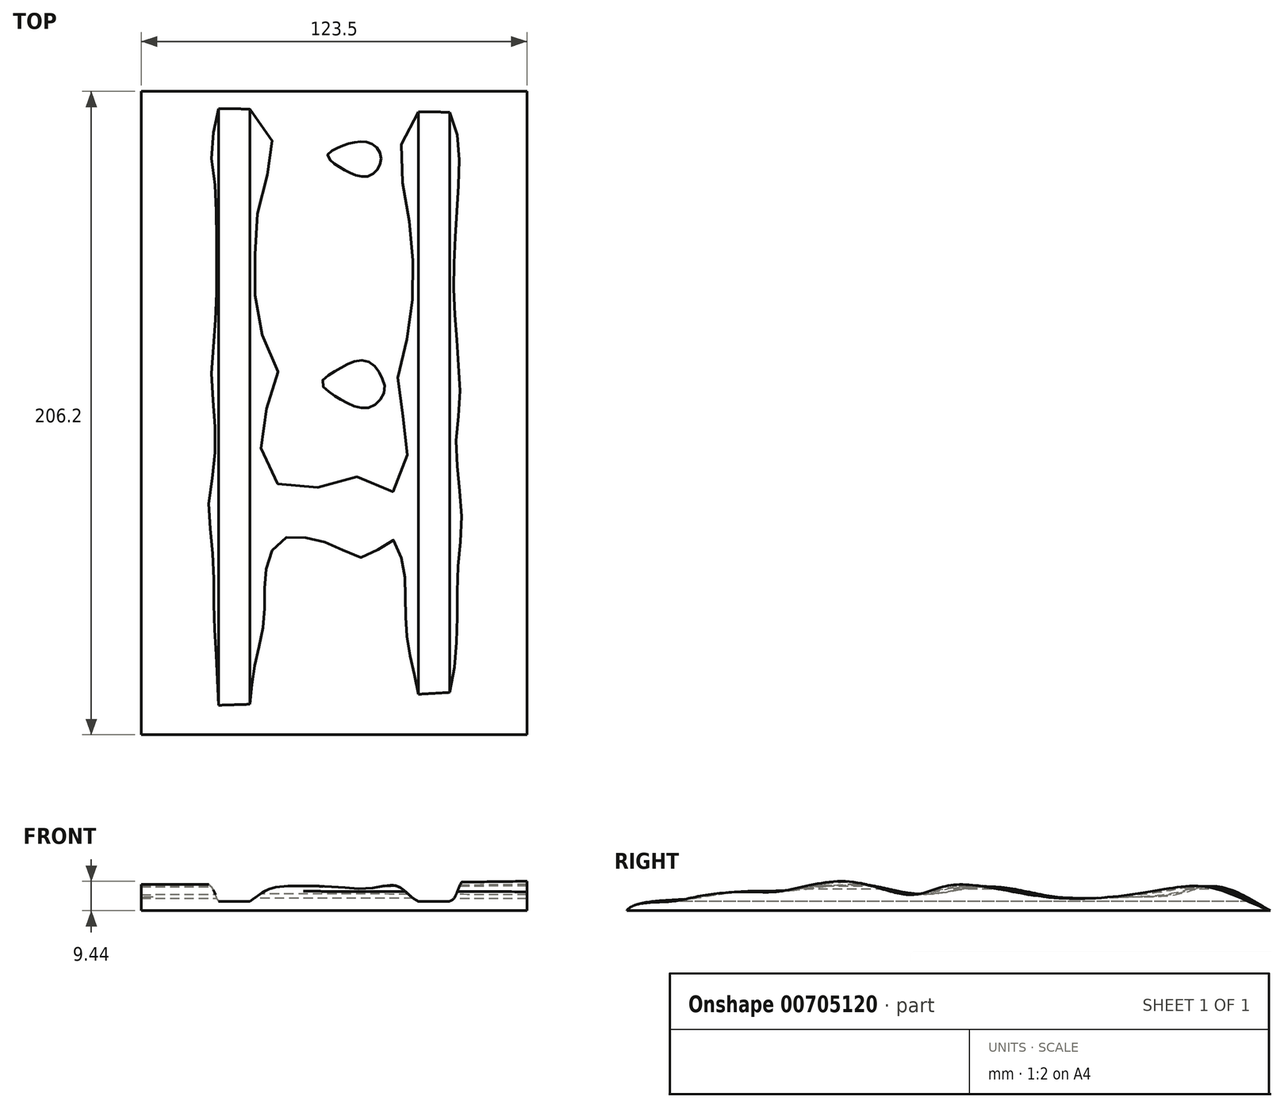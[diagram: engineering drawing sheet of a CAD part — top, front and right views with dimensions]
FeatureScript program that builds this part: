
annotation { "Feature Type Name" : "Feature", "Feature Type Description" : "" }
export const myFeature = defineFeature(function(context is Context, id is Id, definition is map)
    precondition{}
    {
        {
            var Q0;
            Q0=qCreatedBy(makeId("Top.planeOp"),FACE);
            var sketch = newSketch(context, id + "F0", { "sketchPlane" : qUnion([Q0])});
            skLineSegment(sketch, "E0.bottom", {"start": v(-61.75, 103.1) * mm, "end": v(61.75, 103.1) * mm});
            skLineSegment(sketch, "E0.top", {"start": v(-61.75, -103.1) * mm, "end": v(61.75, -103.1) * mm});
            skLineSegment(sketch, "E0.left", {"start": v(-61.75, 103.1) * mm, "end": v(-61.75, -103.1) * mm});
            skLineSegment(sketch, "E0.right", {"start": v(61.75, 103.1) * mm, "end": v(61.75, -103.1) * mm});
            skLineSegment(sketch, "E1", {"start": v(-61.75, -103.1) * mm, "end": v(61.75, 103.1) * mm, "construction": true});
            skSolve(sketch);
        }
        {
            var Q0;
            Q0=qCreatedBy(makeId("Right.planeOp"),FACE);
            var Q1;
            Q1=sQuery(id+"F0.wireOp",VERTEX,"E0.top.end");
            cPlane(context, id + "F1", {"entities" : qUnion([Q0, Q1]), "cplaneType" : CPlaneType.PLANE_POINT, "offset" : 25 * mm, "width" : 150 * mm, "height" : 150 * mm});
        }
        {
            var Q0;
            Q0=qCreatedBy(makeId("Right.planeOp"),FACE);
            var Q1;
            Q1=sQuery(id+"F0.wireOp",VERTEX,"E1.start");
            cPlane(context, id + "F2", {"entities" : qUnion([Q0, Q1]), "cplaneType" : CPlaneType.PLANE_POINT, "offset" : 25 * mm, "width" : 150 * mm, "height" : 150 * mm});
        }
        {
            var Q0;
            Q0=qCreatedBy(makeId("Front.planeOp"),FACE);
            var Q1;
            Q1=sQuery(id+"F0.wireOp",VERTEX,"E0.top.end");
            cPlane(context, id + "F3", {"entities" : qUnion([Q0, Q1]), "cplaneType" : CPlaneType.PLANE_POINT, "offset" : 25 * mm, "width" : 150 * mm, "height" : 150 * mm});
        }
        {
            var Q0;
            Q0=qCreatedBy(id+"F1.planeOp",FACE);
            var sketch = newSketch(context, id + "F4", { "sketchPlane" : qUnion([Q0])});
            skPoint(sketch, "E2.0", {"position": v(-103.1, 0) * mm});
            skLineSegment(sketch, "E3.0", {"start": v(103.1, 0) * mm, "end": v(-103.1, 0) * mm});
            skFitSpline(sketch, "E4", {"points": [v(-103.1, 0) * mm, v(-90, 2.88) * mm, v(-79.4, 4.75) * mm, v(-64.63, 6.07) * mm, v(-53.4, 6.3) * mm, v(-32.22, 9.37) * mm, v(-12.09, 5.07) * mm, v(1.58, 8.28) * mm, v(32.22, 4.27) * mm, v(65.38, 6.24) * mm, v(83.82, 7.43) * mm, v(103.1, 0) * mm], "startDerivative": vector(84.6, 116.32) * mm, "endDerivative": vector(192.63, -70.23) * mm});
            skSolve(sketch);
        }
        {
            var Q0;
            Q0=qCreatedBy(id+"F2.planeOp",FACE);
            var sketch = newSketch(context, id + "F5", { "sketchPlane" : qUnion([Q0])});
            skLineSegment(sketch, "E5.0", {"start": v(103.1, 0) * mm, "end": v(-103.1, 0) * mm});
            skFitSpline(sketch, "E6", {"points": [v(103.1, 0) * mm, v(85.95, 7.8) * mm, v(73.38, 5.16) * mm, v(56.6, 4.36) * mm, v(34.64, 4.36) * mm, v(13.21, 7.67) * mm, v(-8.2, 5.16) * mm, v(-27.25, 8.33) * mm, v(-48.4, 6.61) * mm, v(-66.4, 6.08) * mm, v(-84.38, 3.7) * mm, v(-103.1, 0) * mm], "startDerivative": vector(-178.89, 101.55) * mm, "endDerivative": vector(-86.83, -108.74) * mm});
            skSolve(sketch);
        }
        {
            var Q0;
            Q0=makeQuery(id+"F4.imprint","IMPRINT",FACE,{"disambiguationData":[TD([[makeQuery(id+"F4.imprint","IMPRINT",EDGE,{"derivedFrom":sQuery(id+"F4.wireOp",EDGE,"E3.0")}),-1.0]])]});
            var Q1;
            Q1=makeQuery(id+"F5.imprint","IMPRINT",FACE,{"disambiguationData":[TD([[makeQuery(id+"F5.imprint","IMPRINT",EDGE,{"derivedFrom":sQuery(id+"F5.wireOp",EDGE,"E5.0")}),-1.0]])]});
            loft(context, id + "F6", {"sheetProfilesArray" : [{ "sheetProfileEntities" : qUnion([Q0]) }, { "sheetProfileEntities" : qUnion([Q1]) }]});
        }
        {
            var Q0;
            Q0=qCreatedBy(id+"F3.planeOp",FACE);
            var sketch = newSketch(context, id + "F7", { "sketchPlane" : qUnion([Q0])});
            skLineSegment(sketch, "E7.0", {"start": v(-61.75, 0) * mm, "end": v(61.75, 0) * mm});
            skLineSegment(sketch, "E8", {"start": v(-61.75, 0) * mm, "end": v(-61.75, 26.23) * mm});
            skLineSegment(sketch, "E9", {"start": v(-61.75, 26.23) * mm, "end": v(61.75, 26.23) * mm});
            skLineSegment(sketch, "E10", {"start": v(61.75, 26.23) * mm, "end": v(61.75, 0) * mm});
            skLineSegment(sketch, "E11", {"start": v(-37, 3) * mm, "end": v(-27, 3) * mm});
            skLineSegment(sketch, "E12", {"start": v(-27, 3) * mm, "end": v(27, 3) * mm, "construction": true});
            skLineSegment(sketch, "E13", {"start": v(27, 3) * mm, "end": v(37, 3) * mm});
            skLineSegment(sketch, "E14", {"start": v(0, 0) * mm, "end": v(0, 3) * mm, "construction": true});
            skFitSpline(sketch, "E15", {"points": [v(-37, 3) * mm, v(-40.13, 8.4) * mm, v(-53.08, 9.81) * mm, v(-61.75, 12.61) * mm], "startDerivative": vector(-10.62, 13.07) * mm, "endDerivative": vector(-27.6, 2.06) * mm});
            skFitSpline(sketch, "E16", {"points": [v(-27, 3) * mm, v(-21.48, 6.64) * mm, v(-12.88, 7.94) * mm, v(0.26, 7.61) * mm, v(12.38, 7.27) * mm, v(20.33, 7.81) * mm, v(27, 3) * mm], "startDerivative": vector(28.12, 15.05) * mm, "endDerivative": vector(44.04, -16.65) * mm});
            skLineSegment(sketch, "E17", {"start": v(-27, 3) * mm, "end": v(-27, 11) * mm, "construction": true});
            skLineSegment(sketch, "E18", {"start": v(-27, 11) * mm, "end": v(27, 11) * mm, "construction": true});
            skLineSegment(sketch, "E19", {"start": v(27, 11) * mm, "end": v(27, 3) * mm, "construction": true});
            skFitSpline(sketch, "E20", {"points": [v(37, 3) * mm, v(38.7, 4.44) * mm, v(41.9, 10.42) * mm, v(53.75, 12.58) * mm, v(61.75, 13.96) * mm, v(61.75, 13.92) * mm], "startDerivative": vector(12.8, 6.6) * mm, "endDerivative": vector(-0.91, -2.25) * mm});
            skSolve(sketch);
        }
        {
            var Q0;
            {var subQ1=sQuery(id+"F7.wireOp",EDGE,"E9");Q0=makeQuery(id+"F7.imprint","IMPRINT",FACE,{"disambiguationData":[TD([[makeQuery(id+"F7.imprint","IMPRINT",EDGE,{"derivedFrom":subQ1}),-1.0]])]});}
            extrude(context, id + "F8", {"entities" : qUnion([Q0]), "operationType" : NewBodyOperationType.REMOVE, "endBound" : BoundingType.THROUGH_ALL, "oppositeDirection" : true, "depth" : 25 * mm, "offsetDistance" : 25 * mm});
        }
    });
